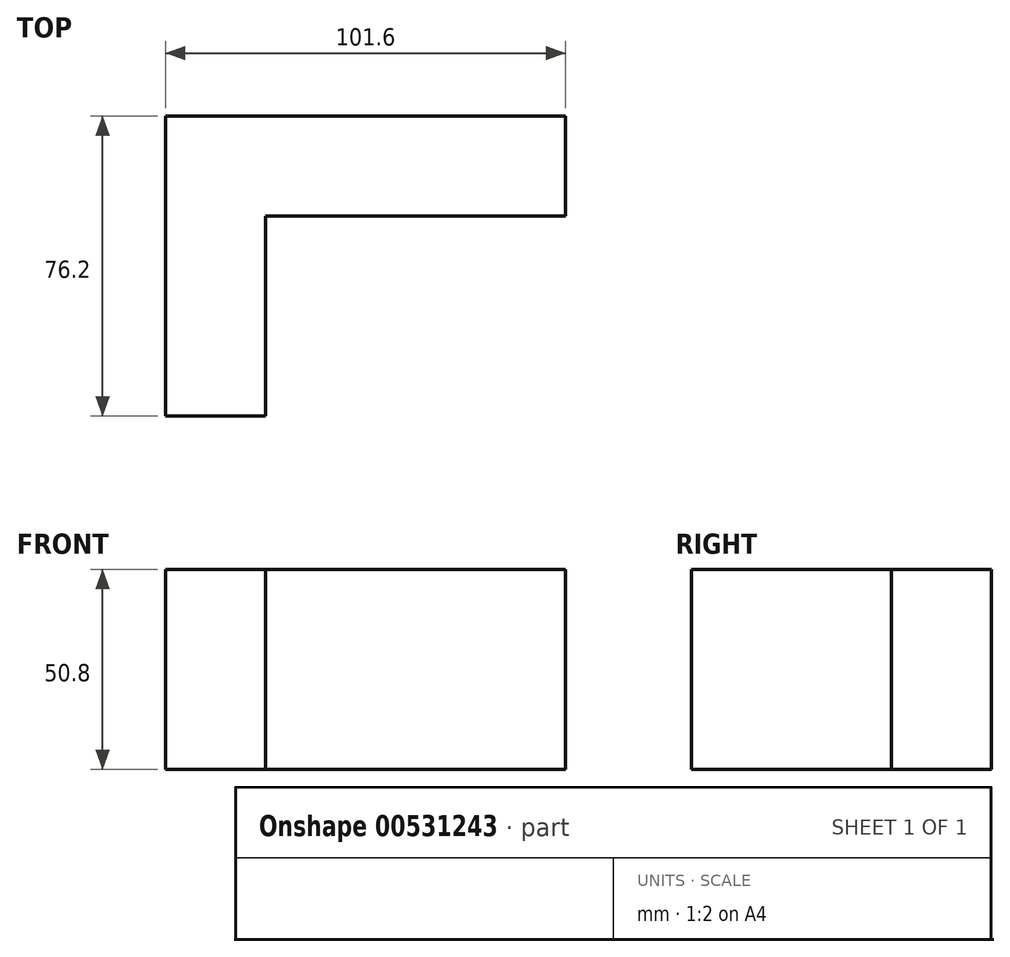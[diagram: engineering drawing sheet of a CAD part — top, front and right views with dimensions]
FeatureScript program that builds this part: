
annotation { "Feature Type Name" : "Feature", "Feature Type Description" : "" }
export const myFeature = defineFeature(function(context is Context, id is Id, definition is map)
    precondition{}
    {
        {
            var Q0;
            Q0=qCreatedBy(makeId("Top.planeOp"),FACE);
            var sketch = newSketch(context, id + "F0", { "sketchPlane" : qUnion([Q0])});
            skLineSegment(sketch, "E0", {"start": v(-84, -62.94) * mm, "end": v(-84, 13.26) * mm});
            skLineSegment(sketch, "E1", {"start": v(-84, 13.26) * mm, "end": v(68.4, 13.26) * mm});
            skLineSegment(sketch, "E2", {"start": v(68.4, 13.26) * mm, "end": v(68.4, -12.14) * mm});
            skLineSegment(sketch, "E3", {"start": v(68.4, -12.14) * mm, "end": v(-58.6, -12.14) * mm});
            skLineSegment(sketch, "E4", {"start": v(-58.6, -12.14) * mm, "end": v(-58.6, -62.94) * mm});
            skLineSegment(sketch, "E5", {"start": v(-58.6, -62.94) * mm, "end": v(-84, -62.94) * mm});
            skLineSegment(sketch, "E6.bottom", {"start": v(17.6, 13.26) * mm, "end": v(68.4, 13.26) * mm});
            skLineSegment(sketch, "E6.top", {"start": v(17.6, -12.14) * mm, "end": v(68.4, -12.14) * mm});
            skLineSegment(sketch, "E6.left", {"start": v(17.6, 13.26) * mm, "end": v(17.6, -12.14) * mm});
            skSolve(sketch);
        }
        {
            var Q0;
            Q0=makeQuery(id+"F0.imprint","IMPRINT",FACE,{"disambiguationData":[TD([[makeQuery(id+"F0.imprint","IMPRINT",EDGE,{"derivedFrom":sQuery(id+"F0.wireOp",EDGE,"E6.bottom")}),-1.0]])]});
            var Q1;
            Q1=makeQuery(id+"F0.imprint","IMPRINT",FACE,{"disambiguationData":[TD([[makeQuery(id+"F0.imprint","IMPRINT",EDGE,{"derivedFrom":sQuery(id+"F0.wireOp",EDGE,"E0")}),-1.0]])]});
            extrude(context, id + "F1", {"entities" : qUnion([Q0, Q1]), "depth" : 50.8 * mm, "offsetDistance" : 25.4 * mm});
        }
    });
